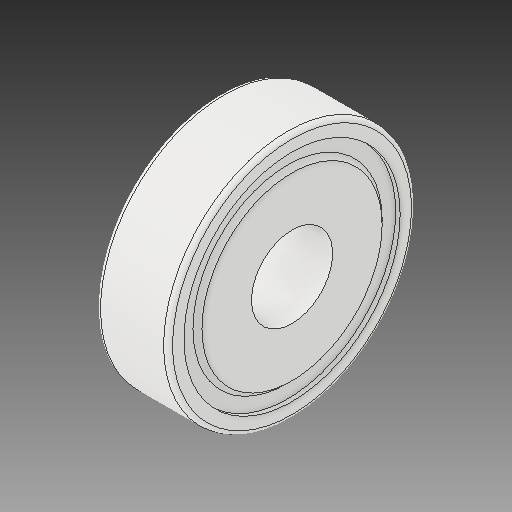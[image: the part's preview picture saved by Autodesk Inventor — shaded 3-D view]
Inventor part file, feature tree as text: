
AUTODESK INVENTOR PART (.ipt)
format: ipt  version: 2019 (Build 230136000, 136)  size: 182,272 bytes
history: native  units: mm
features: extrude x2, sketch x2, mirror x1, fillet x1
ambient origin geometry x8: Origin, YZ Plane, XZ Plane, XY Plane, X Axis, Y Axis, Z Axis, Center Point
bodies: Body1 (feature_tree)
feature tree (6):
  extrude  "Extrusion1"  Depth=55.0mm
  extrude  "Extrusion2"  Depth=1.0mm
  mirror  "Mirror1"
  fillet  "Fillet1"  Radius=40.0mm
  sketch  "Sketch1"  dims[d1=18.0mm d2=55.0mm]
  sketch  "Sketch2"  dims[d3=16.0mm d4=0.0mm d5=48.0mm d6=40.0mm d7=1.0mm d8=0.0mm d9=1.0mm]
